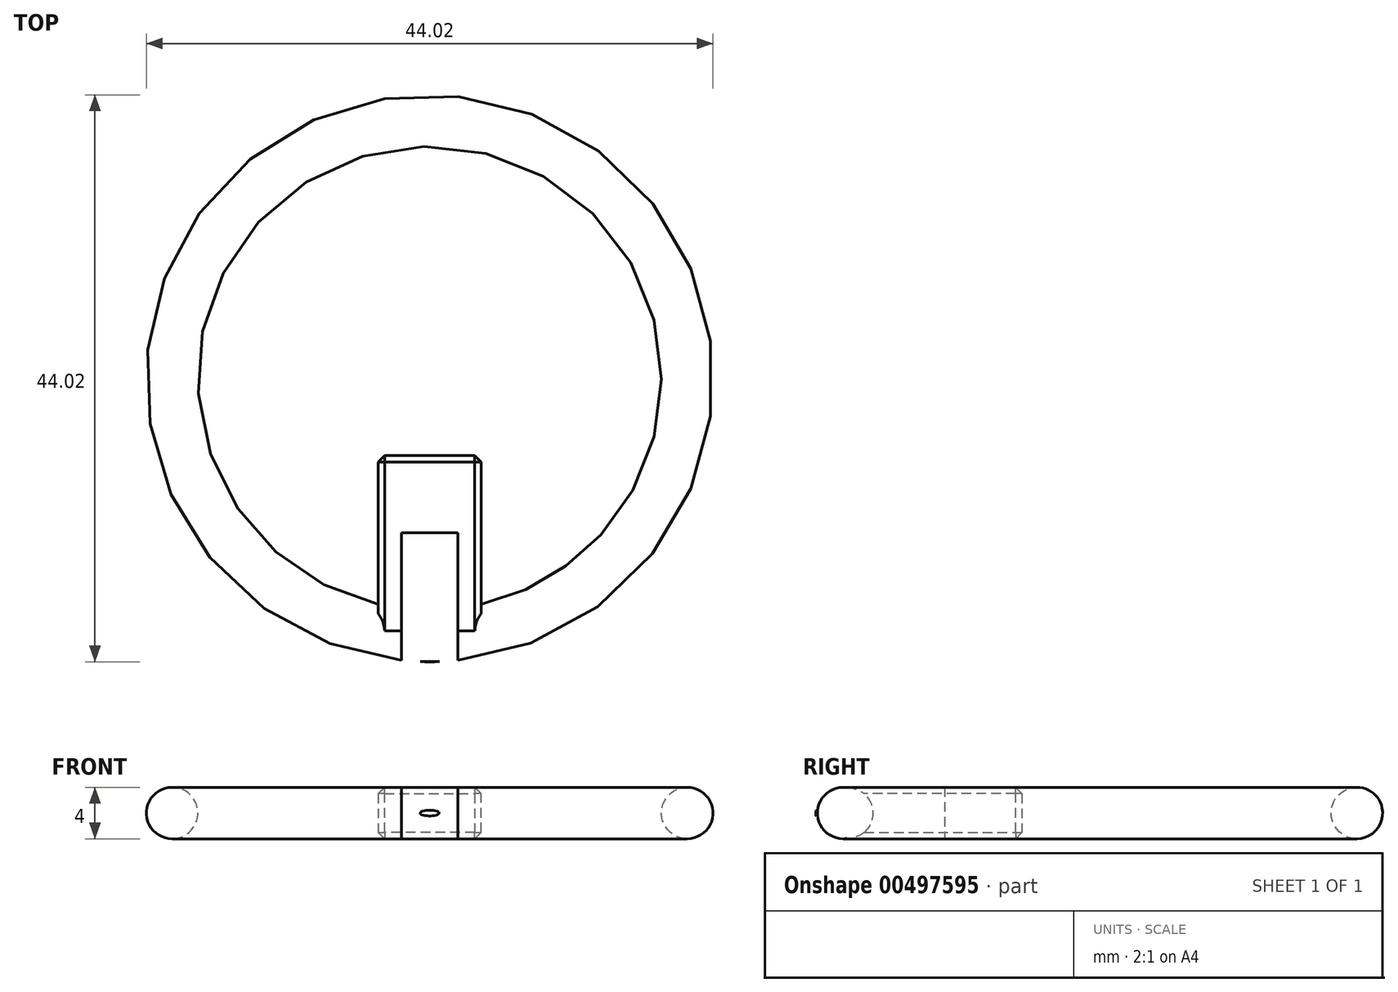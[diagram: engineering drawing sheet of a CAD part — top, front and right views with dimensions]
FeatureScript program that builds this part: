
annotation { "Feature Type Name" : "Feature", "Feature Type Description" : "" }
export const myFeature = defineFeature(function(context is Context, id is Id, definition is map)
    precondition{}
    {
        {
            var Q0;
            Q0=qCreatedBy(makeId("Top.planeOp"),FACE);
            var sketch = newSketch(context, id + "F0", { "sketchPlane" : qUnion([Q0])});
            skLineSegment(sketch, "E0", {"start": v(4, -8) * mm, "end": v(-4, -8) * mm});
            skLineSegment(sketch, "E1", {"start": v(-4, -8) * mm, "end": v(-4, -19.6) * mm});
            skLineSegment(sketch, "E2", {"start": v(-4, -19.6) * mm, "end": v(4, -19.6) * mm});
            skLineSegment(sketch, "E3", {"start": v(4, -19.6) * mm, "end": v(4, -8) * mm});
            skCircle(sketch, "E4", {"center": v(0, 0) * mm, "radius": 20 * mm});
            skLineSegment(sketch, "E5", {"start": v(-4, -8) * mm, "end": v(-4, -6) * mm});
            skLineSegment(sketch, "E6", {"start": v(-4, -6) * mm, "end": v(4, -6) * mm});
            skLineSegment(sketch, "E7", {"start": v(4, -6) * mm, "end": v(4, -8) * mm});
            skSolve(sketch);
        }
        {
            var Q0;
            Q0=qCreatedBy(makeId("Front.planeOp"),FACE);
            var sketch = newSketch(context, id + "F1", { "sketchPlane" : qUnion([Q0])});
            skCircle(sketch, "E8", {"center": v(20.01, 0) * mm, "radius": 2 * mm});
            skSolve(sketch);
        }
        {
            var Q0;
            Q0=makeQuery(id+"F1.imprint","IMPRINT",FACE,{"disambiguationData":[TD([[makeQuery(id+"F1.imprint","IMPRINT",EDGE,{"derivedFrom":sQuery(id+"F1.wireOp",EDGE,"E8")}),1.0]])]});
            var Q1;
            Q1=sQuery(id+"F0.wireOp",EDGE,"E4");
            revolve(context, id + "F2", {"entities" : qUnion([Q0]), "axis" : qUnion([Q1]), "revolveType" : RevolveType.FULL});
        }
        {
            var Q0;
            Q0=makeQuery(id+"F0.imprint","IMPRINT",FACE,{"disambiguationData":[TD([[makeQuery(id+"F0.imprint","IMPRINT",EDGE,{"derivedFrom":sQuery(id+"F0.wireOp",EDGE,"E0")}),1.0]])]});
            var Q1;
            Q1=makeQuery(id+"F0.imprint","IMPRINT",FACE,{"disambiguationData":[TD([[makeQuery(id+"F0.imprint","IMPRINT",EDGE,{"derivedFrom":sQuery(id+"F0.wireOp",EDGE,"E0")}),-1.0]])]});
            extrude(context, id + "F3", {"entities" : qUnion([Q0, Q1]), "operationType" : NewBodyOperationType.ADD, "depth" : 2 * mm, "hasSecondDirection" : true, "secondDirectionOppositeDirection" : true, "secondDirectionDepth" : 2 * mm});
        }
        {
            var Q0;
            Q0=makeQuery(id+"F3.opExtrude","SWEPT_FACE",FACE,{"disambiguationData":[OSD([sQuery(id+"F0.wireOp",EDGE,"E6")])]});
            cPlane(context, id + "F4", {"entities" : qUnion([Q0]), "cplaneType" : CPlaneType.OFFSET, "offset" : 16 * mm, "oppositeDirection" : true, "width" : 150 * mm, "height" : 150 * mm});
        }
        {
            var Q0;
            Q0=qCreatedBy(id+"F4.planeOp",FACE);
            var sketch = newSketch(context, id + "F5", { "sketchPlane" : qUnion([Q0])});
            skLineSegment(sketch, "E9.3", {"start": v(-2.2, -2.08) * mm, "end": v(2.2, -2.08) * mm});
            skLineSegment(sketch, "E9.4", {"start": v(2.2, 2.08) * mm, "end": v(-2.2, 2.08) * mm});
            skLineSegment(sketch, "E10", {"start": v(2.2, 2.08) * mm, "end": v(2.2, -2.08) * mm});
            skLineSegment(sketch, "E11", {"start": v(-2.2, 2.08) * mm, "end": v(-2.2, -2.08) * mm});
            skSolve(sketch);
        }
        {
            var Q0;
            Q0=makeQuery(id+"F5.imprint","IMPRINT",FACE,{"disambiguationData":[TD([[makeQuery(id+"F5.imprint","IMPRINT",EDGE,{"derivedFrom":sQuery(id+"F5.wireOp",EDGE,"E9.3")}),1.0]])]});
            extrude(context, id + "F6", {"entities" : qUnion([Q0]), "operationType" : NewBodyOperationType.REMOVE, "depth" : 10 * mm});
        }
        {
            var Q0;
            Q0=makeQuery(id+"F3.opExtrude","CAP_EDGE",EDGE,{"disambiguationData":[OSD([sQuery(id+"F0.wireOp",EDGE,"E1")])],"isStart":false});
            var Q1;
            Q1=makeQuery(id+"F3.opExtrude","CAP_EDGE",EDGE,{"disambiguationData":[OSD([sQuery(id+"F0.wireOp",EDGE,"E0")])],"isStart":false});
            var Q2;
            Q2=makeQuery(id+"F3.opExtrude","CAP_EDGE",EDGE,{"disambiguationData":[OSD([sQuery(id+"F0.wireOp",EDGE,"E3")])],"isStart":false});
            var Q3;
            Q3=makeQuery(id+"F3.opExtrude","CAP_EDGE",EDGE,{"disambiguationData":[OSD([sQuery(id+"F0.wireOp",EDGE,"E3")])],"isStart":true});
            var Q4;
            Q4=makeQuery(id+"F3.opExtrude","CAP_EDGE",EDGE,{"disambiguationData":[OSD([sQuery(id+"F0.wireOp",EDGE,"E1")])],"isStart":true});
            var Q5;
            Q5=makeQuery(id+"F3.opExtrude","CAP_EDGE",EDGE,{"disambiguationData":[OSD([sQuery(id+"F0.wireOp",EDGE,"E0")])],"isStart":true});
            var Q6;
            Q6=makeQuery(id+"F3.opExtrude","CAP_EDGE",EDGE,{"disambiguationData":[OSD([sQuery(id+"F0.wireOp",EDGE,"E6")])],"isStart":true});
            var Q7;
            Q7=makeQuery(id+"F3.opExtrude","CAP_EDGE",EDGE,{"disambiguationData":[OSD([sQuery(id+"F0.wireOp",EDGE,"E6")])],"isStart":false});
            var Q8;
            Q8=makeQuery(id+"F3.opExtrude","SWEPT_EDGE",EDGE,{"disambiguationData":[OSD([sQuery(id+"F0.wireOp",EDGE,"E6"),sQuery(id+"F0.wireOp",EDGE,"E7")])]});
            var Q9;
            Q9=makeQuery(id+"F3.opExtrude","SWEPT_EDGE",EDGE,{"disambiguationData":[OSD([sQuery(id+"F0.wireOp",EDGE,"E5"),sQuery(id+"F0.wireOp",EDGE,"E6")])]});
            chamfer(context, id + "F7", {"entities" : qUnion([Q0, Q1, Q2, Q3, Q4, Q5, Q6, Q7, Q8, Q9]), "width" : .5 * mm, "tangentPropagation" : true});
        }
    });
